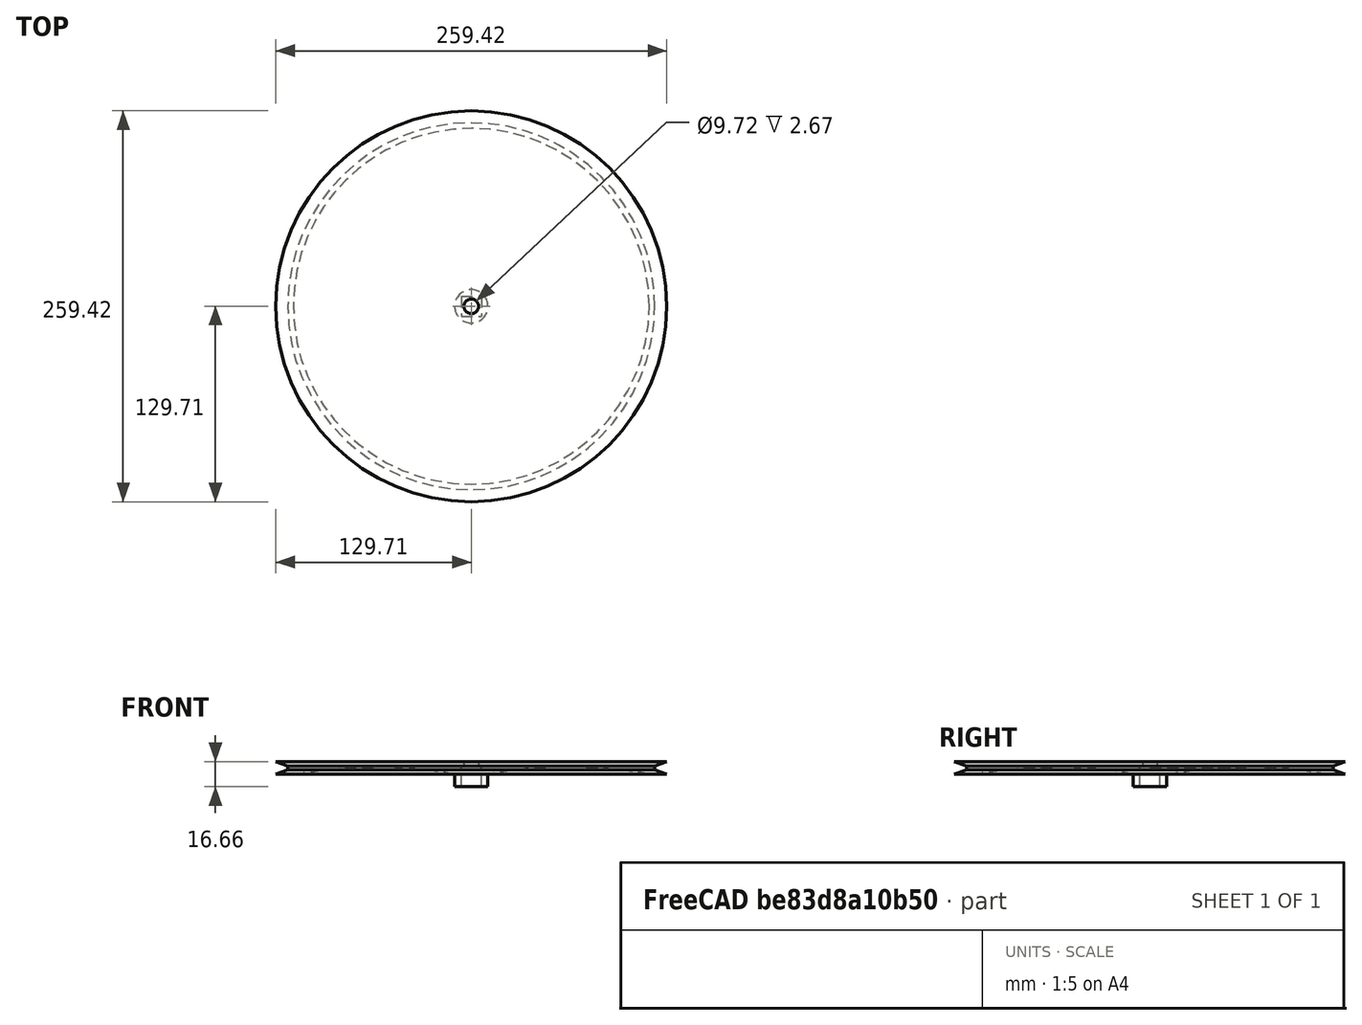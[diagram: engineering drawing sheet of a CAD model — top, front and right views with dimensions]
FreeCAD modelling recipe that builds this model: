
FCSTD DOCUMENT  (FreeCAD 0.18R16110 (Git))
Label: pulley
License: All rights reserved
LicenseURL: http://en.wikipedia.org/wiki/All_rights_reserved
objects: Sketcher::SketchObject×1, Part::Revolution×1, Part::Box×1, Part::Cut×1
note: 4 computed .brp shape members not serialized (recipe doc carries the construction recipe); baked Part::Feature solids carry a one-line shape summary decoded from their .brp

FEATURE [Sketcher::SketchObject] Sketch
  Placement = pos=(0,0,0) rot=(1,0,0;1.5708rad)
  sketch-geometry (16):
    g0: LineSegment StartX=4.86 StartY=10.0107 StartZ=0 EndX=11.05 EndY=10.0107 EndZ=0
    g1: LineSegment StartX=11.05 StartY=10.0107 StartZ=0 EndX=11.05 EndY=18.37 EndZ=0
    g2: LineSegment StartX=118.075 StartY=18.37 StartZ=0 EndX=129.708 EndY=18.37 EndZ=0
    g3: LineSegment StartX=129.708 StartY=18.37 StartZ=0 EndX=121.741 EndY=21.27 EndZ=0
    g4: LineSegment StartX=121.741 StartY=21.27 StartZ=0 EndX=121.741 EndY=23.77 EndZ=0
    g5: LineSegment StartX=121.741 StartY=23.77 StartZ=0 EndX=129.708 EndY=26.67 EndZ=0
    g6: LineSegment StartX=129.708 StartY=26.67 StartZ=0 EndX=4.86 EndY=26.67 EndZ=0
    g7: LineSegment StartX=4.86 StartY=26.67 StartZ=0 EndX=4.86 EndY=10.0107 EndZ=0
    g8: LineSegment [constr] StartX=27.6429 StartY=26.67 StartZ=0 EndX=27.6429 EndY=18.37 EndZ=0
    g9-g12: Circle [constr] x4 (B-spline internal-alignment scaffolding for g13; pole/knot coordinates omitted)
    g13: BSplineCurve PolesCount=4 KnotsCount=2 Degree=3 IsPeriodic=0
    g14: GeomPoint [constr] X=118.075 Y=18.37 Z=0
    g15: GeomPoint [constr] X=11.05 Y=18.37 Z=0
  constraints (34):
    c: Horizontal(g0)
    c: Vertical(g1)
    c: Horizontal(g2)
    c: Coincident(g2,g3)
    c: Coincident(g3,g4)
    c: Vertical(g4)
    c: Coincident(g4,g5)
    c: Equal(g5,g3)
    c: Angle(g3,g5) = 0.698132
    c: Coincident(g5,g6)
    c: Horizontal(g6)
    c: Coincident(g6,g7)
    c: DistanceX(g6) = 4.86
    c: DistanceX(g0) = 4.86
    c: Coincident(g7,g0)
    c: DistanceX(g0) = 11.05
    c: PointOnObject(g8,g6)
    c: PointOnObject(g8,g2)
    c: Vertical(g8)
    c: Distance(g8) = 8.3
    c: Angle(g3,g2) = 0.349066
    c: Coincident(g1,g0)
    c: DistanceY(g4,g4) = 2.5
    c: Coincident(g13,g2)
    c: Radius(g9) = 8
    c: Equal(g9,g10)
    c: Equal(g9,g11)
    c: Equal(g9,g12)
    c: Coincident(g13,g1)
    c: InternalAlignment(g9-g12 -> g13) x4
    c: InternalAlignment(g14,g13)
    c: InternalAlignment(g15,g13)
    c: DistanceY(g2) = 18.37
    c: DistanceY(g1) = 18.37
FEATURE [Part::Revolution] Revolve
  Angle = 360
  Axis = (0,0,1)
  Base = (0,0,0)
  FaceMakerClass = Part::FaceMakerBullseye
  Solid = true
  Source = -> Sketch
  Symmetric = false
FEATURE [Part::Box] Box  label="Cube"
  AttacherType = Attacher::AttachEngine3D
  Height = 14
  Length = 13.4
  Placement = pos=(-6.7,-6.7,10) rot=(0,0,1;0rad)
  Width = 13.4
FEATURE [Part::Cut] Cut
  Base = -> Revolve
  Tool = -> Box
